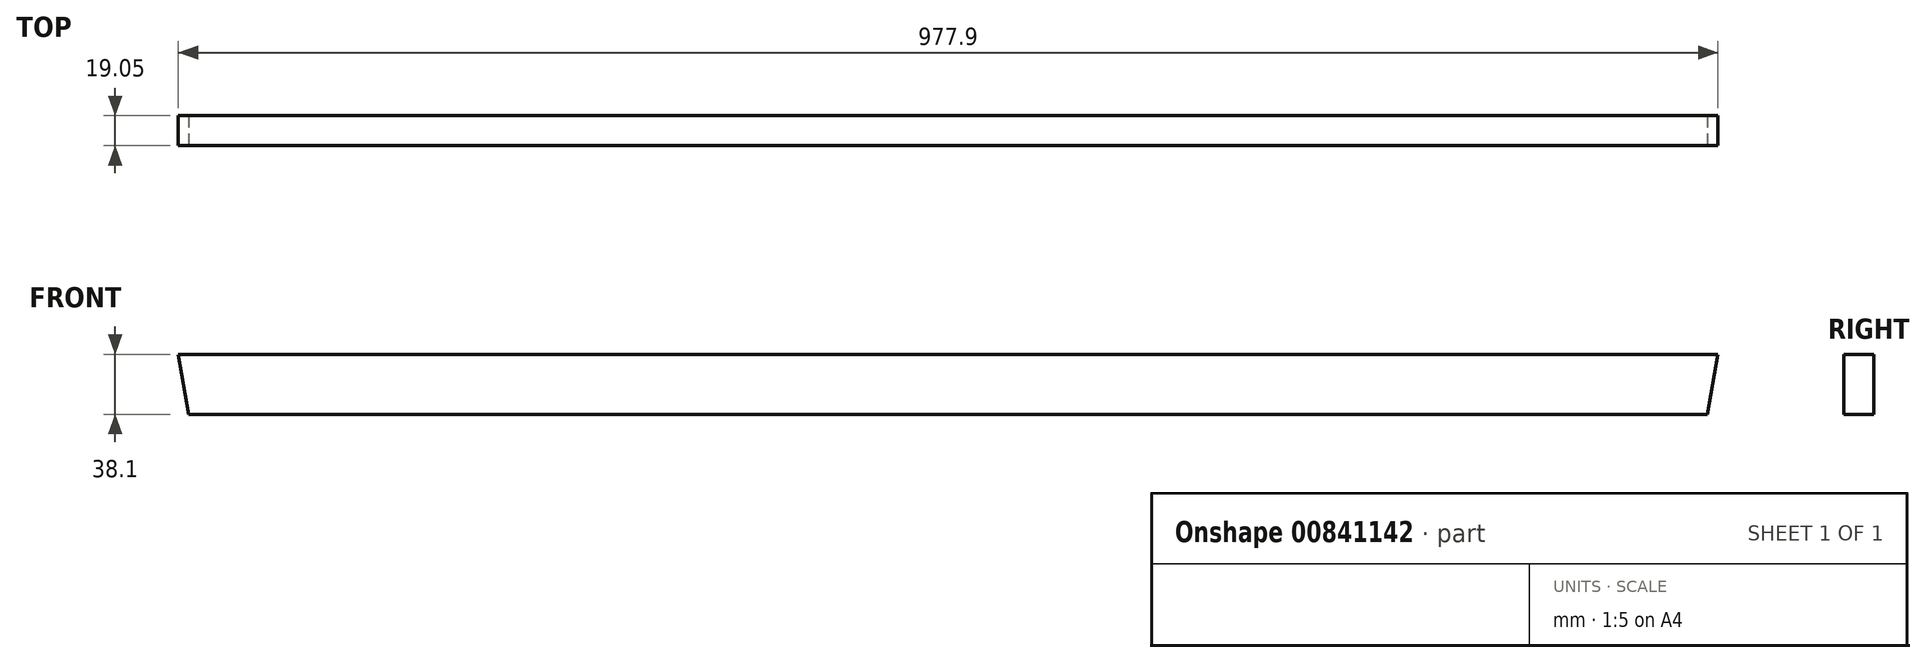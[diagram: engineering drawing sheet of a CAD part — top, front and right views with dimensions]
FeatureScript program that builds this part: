
annotation { "Feature Type Name" : "Feature", "Feature Type Description" : "" }
export const myFeature = defineFeature(function(context is Context, id is Id, definition is map)
    precondition{}
    {
        {
            var Q0;
            Q0=qCreatedBy(makeId("Front.planeOp"),FACE);
            var sketch = newSketch(context, id + "F0", { "sketchPlane" : qUnion([Q0])});
            skLineSegment(sketch, "E0.bottom", {"start": v(0, 0) * mm, "end": v(-977.9, 0) * mm});
            skLineSegment(sketch, "E0.top", {"start": v(0, 38.1) * mm, "end": v(-977.9, 38.1) * mm});
            skLineSegment(sketch, "E0.left", {"start": v(0, 0) * mm, "end": v(0, 38.1) * mm});
            skLineSegment(sketch, "E0.right", {"start": v(-977.9, 0) * mm, "end": v(-977.9, 38.1) * mm});
            skSolve(sketch);
        }
        {
            var Q0;
            Q0=makeQuery(id+"F0.imprint","IMPRINT",FACE,{"disambiguationData":[TD([[makeQuery(id+"F0.imprint","IMPRINT",EDGE,{"derivedFrom":sQuery(id+"F0.wireOp",EDGE,"E0.bottom")}),-1.0]])]});
            extrude(context, id + "F1", {"entities" : qUnion([Q0]), "depth" : 19.05 * mm, "offsetDistance" : 25.4 * mm});
        }
        {
            var Q0;
            Q0=makeQuery(id+"F1.opExtrude","CAP_FACE",FACE,{"disambiguationData":[OSD([sQuery(id+"F0.wireOp",EDGE,"E0.bottom"),sQuery(id+"F0.wireOp",EDGE,"E0.top"),sQuery(id+"F0.wireOp",EDGE,"E0.left"),sQuery(id+"F0.wireOp",EDGE,"E0.right")])],"isStart":false});
            var sketch = newSketch(context, id + "F2", { "sketchPlane" : qUnion([Q0])});
            skLineSegment(sketch, "E1", {"start": v(-977.9, 38.1) * mm, "end": v(-977.9, 0) * mm});
            skLineSegment(sketch, "E2", {"start": v(-977.9, 0) * mm, "end": v(-971.18, 0) * mm});
            skLineSegment(sketch, "E3", {"start": v(-971.18, 0) * mm, "end": v(-977.9, 38.1) * mm});
            skSolve(sketch);
        }
        {
            var Q0;
            Q0=qSketchRegion(id+"F2",true);
            extrude(context, id + "F3", {"entities" : qUnion([Q0]), "operationType" : NewBodyOperationType.REMOVE, "oppositeDirection" : true, "depth" : 25.4 * mm, "offsetDistance" : 25.4 * mm});
        }
        {
            var Q0;
            Q0=makeQuery(id+"F1.opExtrude","CAP_FACE",FACE,{"disambiguationData":[OSD([sQuery(id+"F0.wireOp",EDGE,"E0.bottom"),sQuery(id+"F0.wireOp",EDGE,"E0.top"),sQuery(id+"F0.wireOp",EDGE,"E0.left"),sQuery(id+"F0.wireOp",EDGE,"E0.right")])],"isStart":false});
            var sketch = newSketch(context, id + "F4", { "sketchPlane" : qUnion([Q0])});
            skLineSegment(sketch, "E4", {"start": v(0, 38.1) * mm, "end": v(-6.72, 0) * mm});
            skLineSegment(sketch, "E5", {"start": v(-6.72, 0) * mm, "end": v(0, 0) * mm});
            skLineSegment(sketch, "E6", {"start": v(0, 0) * mm, "end": v(0, 38.1) * mm});
            skSolve(sketch);
        }
        {
            var Q0;
            Q0=qSketchRegion(id+"F4",true);
            extrude(context, id + "F5", {"entities" : qUnion([Q0]), "operationType" : NewBodyOperationType.REMOVE, "oppositeDirection" : true, "depth" : 25.4 * mm, "offsetDistance" : 25.4 * mm});
        }
    });
